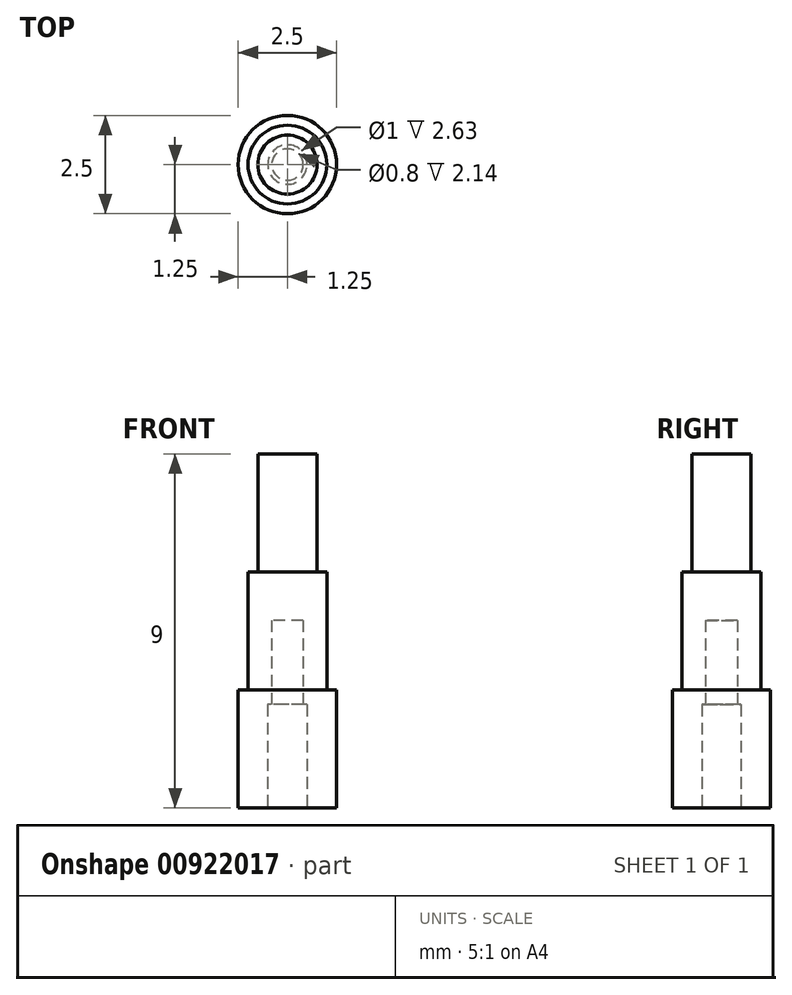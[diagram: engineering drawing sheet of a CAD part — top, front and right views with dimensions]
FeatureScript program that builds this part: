
annotation { "Feature Type Name" : "Feature", "Feature Type Description" : "" }
export const myFeature = defineFeature(function(context is Context, id is Id, definition is map)
    precondition{}
    {
        {
            var Q0;
            Q0=qCreatedBy(makeId("Top.planeOp"),FACE);
            var sketch = newSketch(context, id + "F0", { "sketchPlane" : qUnion([Q0])});
            skCircle(sketch, "E0", {"center": v(0, 0) * mm, "radius": 0.75 * mm});
            skSolve(sketch);
        }
        {
            var Q0;
            Q0=qCreatedBy(makeId("Top.planeOp"),FACE);
            var sketch = newSketch(context, id + "F1", { "sketchPlane" : qUnion([Q0])});
            skCircle(sketch, "E1", {"center": v(0, 0) * mm, "radius": 1 * mm});
            skSolve(sketch);
        }
        {
            var Q0;
            Q0=qSketchRegion(id+"F1",true);
            extrude(context, id + "F2", {"entities" : qUnion([Q0]), "depth" : 6 * mm, "offsetDistance" : 25 * mm});
        }
        {
            var Q0;
            Q0=qSketchRegion(id+"F0",true);
            extrude(context, id + "F3", {"entities" : qUnion([Q0]), "operationType" : NewBodyOperationType.ADD, "depth" : 9 * mm, "offsetDistance" : 25 * mm});
        }
        {
            var Q0;
            Q0=qCreatedBy(makeId("Top.planeOp"),FACE);
            var sketch = newSketch(context, id + "F4", { "sketchPlane" : qUnion([Q0])});
            skCircle(sketch, "E2", {"center": v(0, 0) * mm, "radius": 0.4 * mm});
            skSolve(sketch);
        }
        {
            var Q0;
            Q0=qCreatedBy(makeId("Top.planeOp"),FACE);
            var sketch = newSketch(context, id + "F5", { "sketchPlane" : qUnion([Q0])});
            skCircle(sketch, "E3", {"center": v(0, 0) * mm, "radius": 1.25 * mm});
            skSolve(sketch);
        }
        {
            var Q0;
            Q0=qSketchRegion(id+"F5",true);
            extrude(context, id + "F6", {"entities" : qUnion([Q0]), "operationType" : NewBodyOperationType.ADD, "depth" : 3 * mm, "offsetDistance" : 25 * mm});
        }
        {
            var Q0;
            Q0=qSketchRegion(id+"F4",true);
            extrude(context, id + "F7", {"entities" : qUnion([Q0]), "operationType" : NewBodyOperationType.REMOVE, "depth" : 2.36 * mm, "offsetDistance" : 25 * mm});
        }
        {
            var Q0;
            Q0=qCreatedBy(makeId("Top.planeOp"),FACE);
            var sketch = newSketch(context, id + "F8", { "sketchPlane" : qUnion([Q0])});
            skCircle(sketch, "E4", {"center": v(0, 0) * mm, "radius": 0.5 * mm});
            skSolve(sketch);
        }
        {
            var Q0;
            Q0=qSketchRegion(id+"F8",true);
            extrude(context, id + "F9", {"entities" : qUnion([Q0]), "operationType" : NewBodyOperationType.REMOVE, "depth" : 2.63 * mm, "offsetDistance" : 25 * mm});
        }
        {
            var Q0;
            Q0=qCreatedBy(makeId("Top.planeOp"),FACE);
            var sketch = newSketch(context, id + "F10", { "sketchPlane" : qUnion([Q0])});
            skCircle(sketch, "E5", {"center": v(0, 0) * mm, "radius": 0.4 * mm});
            skSolve(sketch);
        }
        {
            var Q0;
            Q0=qSketchRegion(id+"F10",true);
            extrude(context, id + "F11", {"entities" : qUnion([Q0]), "operationType" : NewBodyOperationType.REMOVE, "depth" : 4.77 * mm, "offsetDistance" : 25 * mm});
        }
    });
